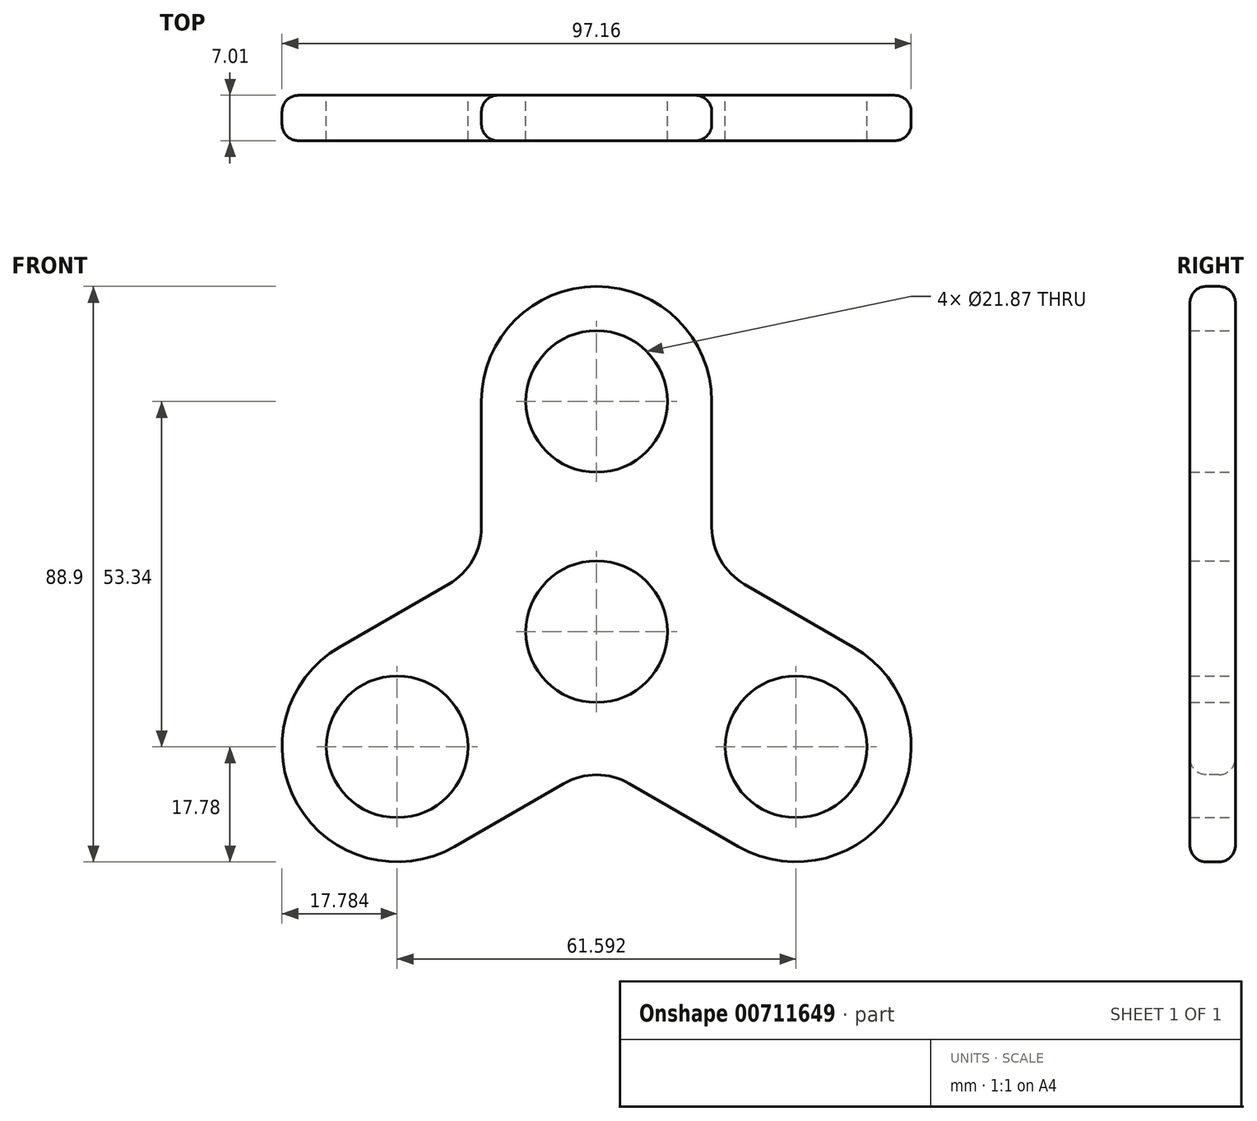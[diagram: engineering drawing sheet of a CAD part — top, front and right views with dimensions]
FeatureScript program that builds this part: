
annotation { "Feature Type Name" : "Feature", "Feature Type Description" : "" }
export const myFeature = defineFeature(function(context is Context, id is Id, definition is map)
    precondition{}
    {
        {
            var Q0;
            Q0=qCreatedBy(makeId("Front.planeOp"),FACE);
            var sketch = newSketch(context, id + "F0", { "sketchPlane" : qUnion([Q0])});
            skCircle(sketch, "E0", {"center": v(0, 0) * mm, "radius": 20.53 * mm, "construction": true});
            skLineSegment(sketch, "E1", {"start": v(-17.78, 10.27) * mm, "end": v(-17.78, 35.56) * mm});
            skCircle(sketch, "E2.cCircle", {"center": v(0, 0) * mm, "radius": 10.27 * mm, "construction": true});
            skLineSegment(sketch, "E2.0", {"start": v(-17.78, 10.27) * mm, "end": v(17.78, 10.27) * mm, "construction": true});
            skLineSegment(sketch, "E2.1", {"start": v(17.78, 10.27) * mm, "end": v(0, -20.53) * mm, "construction": true});
            skLineSegment(sketch, "E2.2", {"start": v(0, -20.53) * mm, "end": v(-17.78, 10.27) * mm, "construction": true});
            skPoint(sketch, "E2.0.midPoint", {"position": v(0, 10.27) * mm});
            skArc(sketch, "E3", {"start": v(17.78, 35.56) * mm, "mid": v(0, 53.34) * mm, "end": v(-17.78, 35.56) * mm});
            skLineSegment(sketch, "E4", {"start": v(17.78, 35.56) * mm, "end": v(17.78, 10.27) * mm});
            skArc(sketch, "E5.1.0", {"start": v(-39.69, -2.38) * mm, "mid": v(-46.2, -26.67) * mm, "end": v(-21.9, -33.18) * mm});
            skLineSegment(sketch, "E5.1.1", {"start": v(0, -20.53) * mm, "end": v(-21.9, -33.18) * mm});
            skLineSegment(sketch, "E5.1.2", {"start": v(-39.69, -2.38) * mm, "end": v(-17.78, 10.27) * mm});
            skArc(sketch, "E5.2.0", {"start": v(21.9, -33.18) * mm, "mid": v(46.2, -26.67) * mm, "end": v(39.69, -2.38) * mm});
            skLineSegment(sketch, "E5.2.1", {"start": v(17.78, 10.27) * mm, "end": v(39.69, -2.38) * mm});
            skLineSegment(sketch, "E5.2.2", {"start": v(21.9, -33.18) * mm, "end": v(0, -20.53) * mm});
            skCircle(sketch, "E6", {"center": v(0, 0) * mm, "radius": 10.94 * mm});
            skCircle(sketch, "E7", {"center": v(0, 35.56) * mm, "radius": 10.94 * mm});
            skCircle(sketch, "E8.1.0", {"center": v(-30.8, -17.78) * mm, "radius": 10.94 * mm});
            skCircle(sketch, "E8.2.0", {"center": v(30.8, -17.78) * mm, "radius": 10.94 * mm});
            skSolve(sketch);
        }
        {
            var Q0;
            Q0 = qSketchRegion(id + "F0", true);
            extrude(context, id + "F1", {"entities" : qUnion([Q0]), "depth" : 7 * mm, "offsetDistance" : 25.4 * mm});
        }
        {
            var Q0;
            Q0=makeQuery(id+"F1.opExtrude","SWEPT_EDGE",EDGE,{"disambiguationData":[OSD([sQuery(id+"F0.wireOp",EDGE,"E4"),sQuery(id+"F0.wireOp",EDGE,"E5.2.1")])]});
            var Q1;
            Q1=makeQuery(id+"F1.opExtrude","SWEPT_EDGE",EDGE,{"disambiguationData":[OSD([sQuery(id+"F0.wireOp",EDGE,"E1"),sQuery(id+"F0.wireOp",EDGE,"E5.1.2")])]});
            var Q2;
            Q2=makeQuery(id+"F1.opExtrude","SWEPT_EDGE",EDGE,{"disambiguationData":[OSD([sQuery(id+"F0.wireOp",EDGE,"E5.1.1"),sQuery(id+"F0.wireOp",EDGE,"E5.2.2")])]});
            fillet(context, id + "F2", {"entities" : qUnion([Q0, Q1, Q2]), "radius" : 10.16 * mm, "tangentPropagation" : true, "allowEdgeOverflow" : false});
        }
        {
            var Q0;
            Q0=makeQuery(id+"F1.opExtrude","CAP_EDGE",EDGE,{"disambiguationData":[OSD([sQuery(id+"F0.wireOp",EDGE,"E1")])],"isStart":false});
            var Q1;
            Q1=makeQuery(id+"F1.opExtrude","CAP_EDGE",EDGE,{"disambiguationData":[OSD([sQuery(id+"F0.wireOp",EDGE,"E1")])],"isStart":true});
            fillet(context, id + "F3", {"entities" : qUnion([Q0, Q1]), "radius" : 2.54 * mm, "tangentPropagation" : true, "allowEdgeOverflow" : false});
        }
    });
